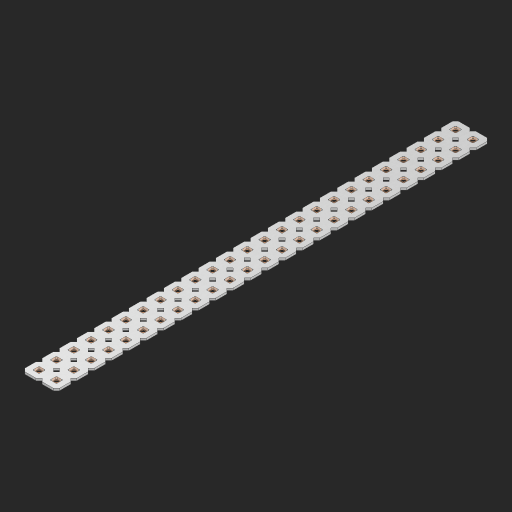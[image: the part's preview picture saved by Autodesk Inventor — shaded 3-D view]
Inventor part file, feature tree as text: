
AUTODESK INVENTOR PART (.ipt)
format: ipt  version: 2023 (Build 270158000, 158)  size: 769,024 bytes
history: native  units: in
note: dims shown in document units (in); Inventor stores cm internally (conversion verified against a paired STEP export)
features: other x51, extrude x49, sketch x2, pattern_linear x1
ambient origin geometry x8: Origin, YZ Plane, XZ Plane, XY Plane, X Axis, Y Axis, Z Axis, Center Point
bodies: Solid1 (feature_tree), Body (feature_tree)
feature tree (103):
  pattern_linear  "Rectangular Pattern1"  Spacing1=0.09in  [1 undecoded]
  sketch  "Sketch1"  dims[d1=0.5in]
  sketch  "Sketch2"  dims[d2=0.182in d3=0.09in d4=0.09in d5=0.09in d6=0.09in d7=0.09in d8=0.09in d9=0.09in d10=0.09in d11=0.02in d13=0.0in d14=0.172in d15=0.0625in d16=0.0in d19=0.5in d22=0.5in]
  other  "Srf1"
  other  "Srf126"
  other  "Srf127"
  other  "Srf128"
  other  "Srf129"
  other  "Srf130"
  other  "Srf131"
  other  "Srf250"
  other  "Srf251"
  other  "Srf252"
  other  "Srf253"
  other  "Srf254"
  other  "Srf255"
  other  "Srf256"
  other  "Srf257"
  other  "Srf258"
  other  "Srf259"
  other  "Srf260"
  other  "Srf261"
  other  "Srf262"
  other  "Srf263"
  other  "Srf264"
  other  "Srf265"
  other  "Srf266"
  other  "Srf267"
  other  "Srf268"
  other  "Srf269"
  other  "Srf270"
  other  "Srf271"
  other  "Srf272"
  other  "Srf273"
  other  "Srf274"
  other  "Srf275"
  other  "Srf276"
  other  "Srf277"
  other  "Srf278"
  other  "Srf279"
  other  "Srf280"
  other  "Srf281"
  other  "Srf282"
  other  "Srf283"
  other  "Srf284"
  other  "Srf285"
  other  "Srf286"
  other  "Srf287"
  other  "Srf288"
  other  "Srf289"
  other  "Srf290"
  other  "Srf291"
  other  "Srf292"
  other  "Circle"
  extrude  "ExtrusionSrf126"  Depth=0.09in
  extrude  "ExtrusionSrf127"  Depth=0.09in
  extrude  "ExtrusionSrf128"  Depth=0.09in
  extrude  "ExtrusionSrf129"  Depth=0.09in
  extrude  "ExtrusionSrf130"  Depth=0.09in
  extrude  "ExtrusionSrf131"  Depth=0.09in
  extrude  "ExtrusionSrf250"  Depth=0.09in
  extrude  "ExtrusionSrf251"  Depth=0.02in
  extrude  "ExtrusionSrf252"  TaperAngle=0.0deg  [1 undecoded]
  extrude  "ExtrusionSrf253"  Depth=0.5in
  extrude  "ExtrusionSrf254"  Depth=0.0625in TaperAngle=0.0deg
  extrude  "ExtrusionSrf255"  Depth=0.5in
  extrude  "ExtrusionSrf256"  Depth=0.5in
  extrude  "ExtrusionSrf257"  [1 undecoded]
  extrude  "ExtrusionSrf258"  [1 undecoded]
  extrude  "ExtrusionSrf259"  [1 undecoded]
  extrude  "ExtrusionSrf260"  [1 undecoded]
  extrude  "ExtrusionSrf261"  [1 undecoded]
  extrude  "ExtrusionSrf262"  [1 undecoded]
  extrude  "ExtrusionSrf263"  [1 undecoded]
  extrude  "ExtrusionSrf264"  [1 undecoded]
  extrude  "ExtrusionSrf265"  [1 undecoded]
  extrude  "ExtrusionSrf266"  [1 undecoded]
  extrude  "ExtrusionSrf267"  [1 undecoded]
  extrude  "ExtrusionSrf268"  [1 undecoded]
  extrude  "ExtrusionSrf269"  [1 undecoded]
  extrude  "ExtrusionSrf270"  [1 undecoded]
  extrude  "ExtrusionSrf271"  [1 undecoded]
  extrude  "ExtrusionSrf272"  [1 undecoded]
  extrude  "ExtrusionSrf273"  [1 undecoded]
  extrude  "ExtrusionSrf274"  [1 undecoded]
  extrude  "ExtrusionSrf275"  [1 undecoded]
  extrude  "ExtrusionSrf276"  [1 undecoded]
  extrude  "ExtrusionSrf277"  [1 undecoded]
  extrude  "ExtrusionSrf278"  [1 undecoded]
  extrude  "ExtrusionSrf279"  [1 undecoded]
  extrude  "ExtrusionSrf280"  [1 undecoded]
  extrude  "ExtrusionSrf281"  [1 undecoded]
  extrude  "ExtrusionSrf282"  [1 undecoded]
  extrude  "ExtrusionSrf283"  [1 undecoded]
  extrude  "ExtrusionSrf284"  [1 undecoded]
  extrude  "ExtrusionSrf285"  [1 undecoded]
  extrude  "ExtrusionSrf286"  [1 undecoded]
  extrude  "ExtrusionSrf287"  [1 undecoded]
  extrude  "ExtrusionSrf288"  [1 undecoded]
  extrude  "ExtrusionSrf289"  [1 undecoded]
  extrude  "ExtrusionSrf290"  [1 undecoded]
  extrude  "ExtrusionSrf291"  [1 undecoded]
  extrude  "ExtrusionSrf292"  [1 undecoded]
note: 38 required parameter values undecoded (feature->parameter linkage not recoverable at this tier; creation-order binding heuristic only, values carry confidence <= 0.55)
